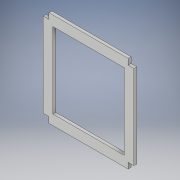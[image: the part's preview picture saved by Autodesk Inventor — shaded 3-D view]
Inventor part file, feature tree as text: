
AUTODESK INVENTOR PART (.ipt)
format: ipt  version: 2018 (Build 220112000, 112)  size: 112,128 bytes
history: native  units: in
note: dims shown in document units (in); Inventor stores cm internally (conversion verified against a paired STEP export)
features: extrude x1, sketch x1
ambient origin geometry x8: Origin, YZ Plane, XZ Plane, XY Plane, X Axis, Y Axis, Z Axis, Center Point
bodies: Solid1 (feature_tree)
feature tree (2):
  extrude  "Extrusion1"  Depth=2.0in
  sketch  "Sketch1"  dims[d0=27.262in d1=2.0in d2=2.0in d3=29.0in d4=2.0in d5=2.0in d6=2.0in d7=2.0in d8=1.0in d9=0.0in]
